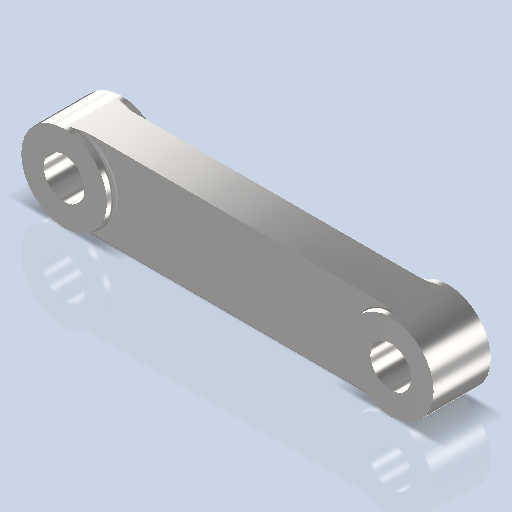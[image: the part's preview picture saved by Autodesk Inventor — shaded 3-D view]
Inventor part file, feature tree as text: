
AUTODESK INVENTOR PART (.ipt)
format: ipt  version: 2024 (Build 280153000, 153)  size: 261,120 bytes
history: native  units: mm
features: sketch x2, extrude x2, hole x2, fillet x1
ambient origin geometry x8: Origin, YZ Plane, XZ Plane, XY Plane, X Axis, Y Axis, Z Axis, Center Point
bodies: Volumenkörper1 (feature_tree)
feature tree (7):
  sketch  "Skizze1"  dims[d1=10.5mm d2=10.5mm]
  extrude  "Extrusion1"  Depth=10.5mm
  extrude  "Extrusion2"  Depth=0.5mm TaperAngle=0.0deg
  sketch  "Skizze2"  dims[d3=40.0mm d4=7.0mm d5=0.0mm d6=5.0mm d7=0.0mm d8=5.0mm d9=6.0mm d10=4.0mm d11=2.0mm d12=90.0deg d13=8.0mm d14=0.0mm d15=5.0mm d16=6.0mm d17=4.0mm d18=2.0mm d19=90.0deg d20=8.0mm d21=0.0mm d22=0.5mm]
  hole  "Bohrung1"  [1 undecoded]
  hole  "Bohrung2"  [1 undecoded]
  fillet  "Rundung1"  [1 undecoded]
note: 3 required parameter values undecoded (feature->parameter linkage not recoverable at this tier; creation-order binding heuristic only, values carry confidence <= 0.55)
